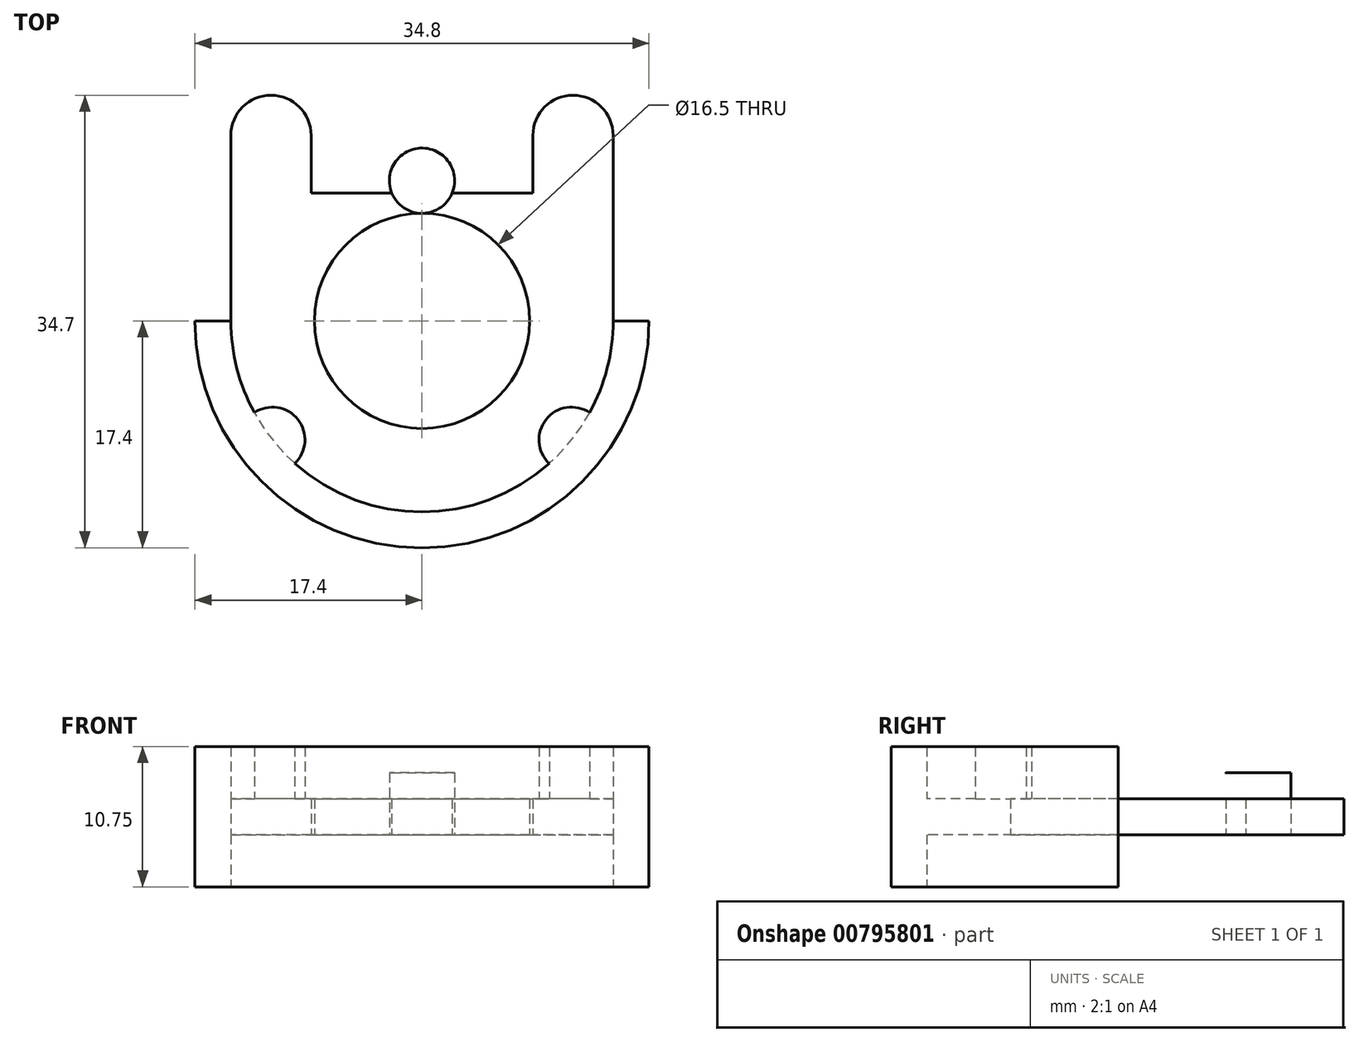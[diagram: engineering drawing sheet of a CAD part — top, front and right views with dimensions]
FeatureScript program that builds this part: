
annotation { "Feature Type Name" : "Feature", "Feature Type Description" : "" }
export const myFeature = defineFeature(function(context is Context, id is Id, definition is map)
    precondition{}
    {
        {
            var Q0;
            Q0=qCreatedBy(makeId("Top.planeOp"),FACE);
            var sketch = newSketch(context, id + "F0", { "sketchPlane" : qUnion([Q0])});
            skCircle(sketch, "E0", {"center": v(0, 0) * mm, "radius": 8.25 * mm});
            skCircle(sketch, "E1.0", {"center": v(0, 0) * mm, "radius": 14.65 * mm});
            skLineSegment(sketch, "E2", {"start": v(14.65, 0) * mm, "end": v(17.4, 0) * mm});
            skLineSegment(sketch, "E3", {"start": v(-14.65, 0) * mm, "end": v(-17.4, 0) * mm});
            skArc(sketch, "E4", {"start": v(-17.4, 0) * mm, "mid": v(0, -17.4) * mm, "end": v(17.4, 0) * mm});
            skLineSegment(sketch, "E5", {"start": v(0, -17.4) * mm, "end": v(0, 9.8) * mm, "construction": true});
            skLineSegment(sketch, "E6", {"start": v(-14.65, 0) * mm, "end": v(-14.65, 9.8) * mm});
            skLineSegment(sketch, "E7", {"start": v(14.65, 0) * mm, "end": v(14.65, 9.8) * mm});
            skLineSegment(sketch, "E8", {"start": v(0, 9.8) * mm, "end": v(8.5, 9.8) * mm});
            skLineSegment(sketch, "E9", {"start": v(0, 9.8) * mm, "end": v(-8.5, 9.8) * mm});
            skLineSegment(sketch, "E10", {"start": v(-8.5, 9.8) * mm, "end": v(-14.65, 9.8) * mm, "construction": true});
            skLineSegment(sketch, "E11", {"start": v(-11.58, 9.8) * mm, "end": v(-11.58, 17.3) * mm, "construction": true});
            skLineSegment(sketch, "E12", {"start": v(-14.65, 9.8) * mm, "end": v(-14.65, 18.1) * mm, "construction": true});
            skLineSegment(sketch, "E13", {"start": v(-11.58, 17.3) * mm, "end": v(-11.58, 14.22) * mm});
            skArc(sketch, "E14", {"start": v(-11.58, 17.3) * mm, "mid": v(-13.75, 16.4) * mm, "end": v(-14.65, 14.22) * mm});
            skArc(sketch, "E15", {"start": v(-11.58, 17.3) * mm, "mid": v(-9.4, 16.4) * mm, "end": v(-8.5, 14.22) * mm});
            skLineSegment(sketch, "E16", {"start": v(-8.5, 14.22) * mm, "end": v(-8.5, 9.8) * mm});
            skLineSegment(sketch, "E17", {"start": v(-14.65, 14.22) * mm, "end": v(-14.65, 9.8) * mm});
            skArc(sketch, "E18.MirrorCS", {"start": v(11.58, 17.3) * mm, "mid": v(9.4, 16.4) * mm, "end": v(8.5, 14.22) * mm});
            skLineSegment(sketch, "E19.MirrorCS", {"start": v(8.5, 14.22) * mm, "end": v(8.5, 9.8) * mm});
            skLineSegment(sketch, "E20.MirrorCS", {"start": v(14.65, 14.22) * mm, "end": v(14.65, 9.8) * mm});
            skArc(sketch, "E21.MirrorCS", {"start": v(11.58, 17.3) * mm, "mid": v(13.75, 16.4) * mm, "end": v(14.65, 14.22) * mm});
            skLineSegment(sketch, "E22", {"start": v(0, 8.25) * mm, "end": v(0, 13.25) * mm, "construction": true});
            skCircle(sketch, "E23", {"center": v(0, 10.75) * mm, "radius": 2.5 * mm});
            skLineSegment(sketch, "E24", {"start": v(0, 10.75) * mm, "end": v(15.54, -16.17) * mm, "construction": true});
            skLineSegment(sketch, "E25", {"start": v(0, 10.75) * mm, "end": v(-15.2, -15.58) * mm, "construction": true});
            skCircle(sketch, "E26", {"center": v(-11.47, -9.11) * mm, "radius": 2.5 * mm});
            skCircle(sketch, "E27", {"center": v(11.47, -9.11) * mm, "radius": 2.5 * mm});
            skSolve(sketch);
        }
        {
            var Q0;
            {var subQ13=sQuery(id+"F0.wireOp",EDGE,"E0");Q0=makeQuery(id+"F0.imprint","IMPRINT",FACE,{"disambiguationData":[TD([[makeQuery(id+"F0.imprint","IMPRINT",EDGE,{"derivedFrom":subQ13}),-1.0]])]});}
            var Q1;
            {var subQ0=sQuery(id+"F0.wireOp",EDGE,"E27");var subQ1=sQuery(id+"F0.wireOp",EDGE,"E1.0");var subQ2=makeQuery(id+"F0.imprint","INTERSECT",VERTEX,{"disambiguationData":[OD(0.0)],"derivedFrom":[subQ1,subQ0]});Q1=makeQuery(id+"F0.imprint","IMPRINT",FACE,{"disambiguationData":[TD([[makeQuery(id+"F0.imprint","IMPRINT",EDGE,{"disambiguationData":[TD([[subQ2,-1.0]])],"derivedFrom":subQ1}),1.0]])]});}
            var Q2;
            {var subQ0=sQuery(id+"F0.wireOp",EDGE,"E26");var subQ1=sQuery(id+"F0.wireOp",EDGE,"E1.0");var subQ2=makeQuery(id+"F0.imprint","INTERSECT",VERTEX,{"disambiguationData":[OD(0.0)],"derivedFrom":[subQ1,subQ0]});Q2=makeQuery(id+"F0.imprint","IMPRINT",FACE,{"disambiguationData":[TD([[makeQuery(id+"F0.imprint","IMPRINT",EDGE,{"disambiguationData":[TD([[subQ2,-1.0]])],"derivedFrom":subQ1}),1.0]])]});}
            var Q3;
            {var subQ4=sQuery(id+"F0.wireOp",EDGE,"E7");Q3=makeQuery(id+"F0.imprint","IMPRINT",FACE,{"disambiguationData":[TD([[makeQuery(id+"F0.imprint","IMPRINT",EDGE,{"derivedFrom":subQ4}),1.0]])]});}
            var Q4;
            {var subQ1=sQuery(id+"F0.wireOp",EDGE,"E6");Q4=makeQuery(id+"F0.imprint","IMPRINT",FACE,{"disambiguationData":[TD([[makeQuery(id+"F0.imprint","IMPRINT",EDGE,{"derivedFrom":subQ1}),-1.0]])]});}
            var Q5;
            {var subQ0=sQuery(id+"F0.wireOp",EDGE,"E9");var subQ1=sQuery(id+"F0.wireOp",EDGE,"E8");var subQ2=makeQuery(id+"F0.imprint","INTERSECT",VERTEX,{"derivedFrom":[subQ1,subQ0]});Q5=makeQuery(id+"F0.imprint","IMPRINT",FACE,{"disambiguationData":[TD([[makeQuery(id+"F0.imprint","IMPRINT",EDGE,{"disambiguationData":[TD([[subQ2,-1.0]])],"derivedFrom":subQ1}),-1.0]])]});}
            var Q6;
            {var subQ0=sQuery(id+"F0.wireOp",EDGE,"E9");var subQ1=sQuery(id+"F0.wireOp",EDGE,"E8");var subQ2=makeQuery(id+"F0.imprint","INTERSECT",VERTEX,{"derivedFrom":[subQ1,subQ0]});Q6=makeQuery(id+"F0.imprint","IMPRINT",FACE,{"disambiguationData":[TD([[makeQuery(id+"F0.imprint","IMPRINT",EDGE,{"disambiguationData":[TD([[subQ2,-1.0]])],"derivedFrom":subQ1}),1.0]])]});}
            extrude(context, id + "F1", {"entities" : qUnion([Q0, Q1, Q2, Q3, Q4, Q5, Q6]), "depth" : 2.75 * mm, "offsetDistance" : 25 * mm});
        }
        {
            var Q0;
            {var subQ0=sQuery(id+"F0.wireOp",EDGE,"E2");Q0=makeQuery(id+"F0.imprint","IMPRINT",FACE,{"disambiguationData":[TD([[makeQuery(id+"F0.imprint","IMPRINT",EDGE,{"derivedFrom":subQ0}),-1.0]])]});}
            var Q1;
            {var subQ0=sQuery(id+"F0.wireOp",EDGE,"E26");var subQ1=sQuery(id+"F0.wireOp",EDGE,"E1.0");var subQ2=makeQuery(id+"F0.imprint","INTERSECT",VERTEX,{"disambiguationData":[OD(0.0)],"derivedFrom":[subQ1,subQ0]});Q1=makeQuery(id+"F0.imprint","IMPRINT",FACE,{"disambiguationData":[TD([[makeQuery(id+"F0.imprint","IMPRINT",EDGE,{"disambiguationData":[TD([[subQ2,-1.0]])],"derivedFrom":subQ1}),-1.0]])]});}
            var Q2;
            {var subQ0=sQuery(id+"F0.wireOp",EDGE,"E27");var subQ1=sQuery(id+"F0.wireOp",EDGE,"E1.0");var subQ2=makeQuery(id+"F0.imprint","INTERSECT",VERTEX,{"disambiguationData":[OD(0.0)],"derivedFrom":[subQ1,subQ0]});Q2=makeQuery(id+"F0.imprint","IMPRINT",FACE,{"disambiguationData":[TD([[makeQuery(id+"F0.imprint","IMPRINT",EDGE,{"disambiguationData":[TD([[subQ2,-1.0]])],"derivedFrom":subQ1}),-1.0]])]});}
            extrude(context, id + "F2", {"entities" : qUnion([Q0, Q1, Q2]), "operationType" : NewBodyOperationType.ADD, "depth" : (2.75 + 4) * mm, "offsetDistance" : 25 * mm, "hasSecondDirection" : true, "secondDirectionOppositeDirection" : true, "secondDirectionDepth" : 4 * mm});
        }
        {
            var Q0;
            {var subQ0=sQuery(id+"F0.wireOp",EDGE,"E27");var subQ1=sQuery(id+"F0.wireOp",EDGE,"E1.0");var subQ2=makeQuery(id+"F0.imprint","INTERSECT",VERTEX,{"disambiguationData":[OD(0.0)],"derivedFrom":[subQ1,subQ0]});Q0=makeQuery(id+"F0.imprint","IMPRINT",FACE,{"disambiguationData":[TD([[makeQuery(id+"F0.imprint","IMPRINT",EDGE,{"disambiguationData":[TD([[subQ2,-1.0]])],"derivedFrom":subQ1}),1.0]])]});}
            var Q1;
            {var subQ0=sQuery(id+"F0.wireOp",EDGE,"E26");var subQ1=sQuery(id+"F0.wireOp",EDGE,"E1.0");var subQ2=makeQuery(id+"F0.imprint","INTERSECT",VERTEX,{"disambiguationData":[OD(0.0)],"derivedFrom":[subQ1,subQ0]});Q1=makeQuery(id+"F0.imprint","IMPRINT",FACE,{"disambiguationData":[TD([[makeQuery(id+"F0.imprint","IMPRINT",EDGE,{"disambiguationData":[TD([[subQ2,-1.0]])],"derivedFrom":subQ1}),1.0]])]});}
            var Q2;
            {var subQ0=sQuery(id+"F0.wireOp",EDGE,"E26");var subQ1=sQuery(id+"F0.wireOp",EDGE,"E1.0");var subQ2=makeQuery(id+"F0.imprint","INTERSECT",VERTEX,{"disambiguationData":[OD(0.0)],"derivedFrom":[subQ1,subQ0]});Q2=makeQuery(id+"F0.imprint","IMPRINT",FACE,{"disambiguationData":[TD([[makeQuery(id+"F0.imprint","IMPRINT",EDGE,{"disambiguationData":[TD([[subQ2,-1.0]])],"derivedFrom":subQ1}),-1.0]])]});}
            var Q3;
            Q3=makeQuery(id+"F2.opExtrude","CAP_FACE",FACE,{"disambiguationData":[OSD([sQuery(id+"F0.wireOp",EDGE,"E1.0"),sQuery(id+"F0.wireOp",EDGE,"E2"),sQuery(id+"F0.wireOp",EDGE,"E3"),sQuery(id+"F0.wireOp",EDGE,"E4")])],"isStart":false});
            extrude(context, id + "F3", {"entities" : qUnion([Q0, Q1, Q2]), "operationType" : NewBodyOperationType.ADD, "endBound" : BoundingType.UP_TO_SURFACE, "depth" : 25 * mm, "endBoundEntityFace" : qUnion([Q3]), "offsetDistance" : 25 * mm});
        }
        {
            var Q0;
            {var subQ0=sQuery(id+"F0.wireOp",EDGE,"E9");var subQ1=sQuery(id+"F0.wireOp",EDGE,"E8");var subQ2=makeQuery(id+"F0.imprint","INTERSECT",VERTEX,{"derivedFrom":[subQ1,subQ0]});Q0=makeQuery(id+"F0.imprint","IMPRINT",FACE,{"disambiguationData":[TD([[makeQuery(id+"F0.imprint","IMPRINT",EDGE,{"disambiguationData":[TD([[subQ2,-1.0]])],"derivedFrom":subQ1}),1.0]])]});}
            var Q1;
            {var subQ0=sQuery(id+"F0.wireOp",EDGE,"E9");var subQ1=sQuery(id+"F0.wireOp",EDGE,"E8");var subQ2=makeQuery(id+"F0.imprint","INTERSECT",VERTEX,{"derivedFrom":[subQ1,subQ0]});Q1=makeQuery(id+"F0.imprint","IMPRINT",FACE,{"disambiguationData":[TD([[makeQuery(id+"F0.imprint","IMPRINT",EDGE,{"disambiguationData":[TD([[subQ2,-1.0]])],"derivedFrom":subQ1}),-1.0]])]});}
            extrude(context, id + "F4", {"entities" : qUnion([Q0, Q1]), "operationType" : NewBodyOperationType.ADD, "depth" : 4.75 * mm, "offsetDistance" : 25 * mm});
        }
    });
